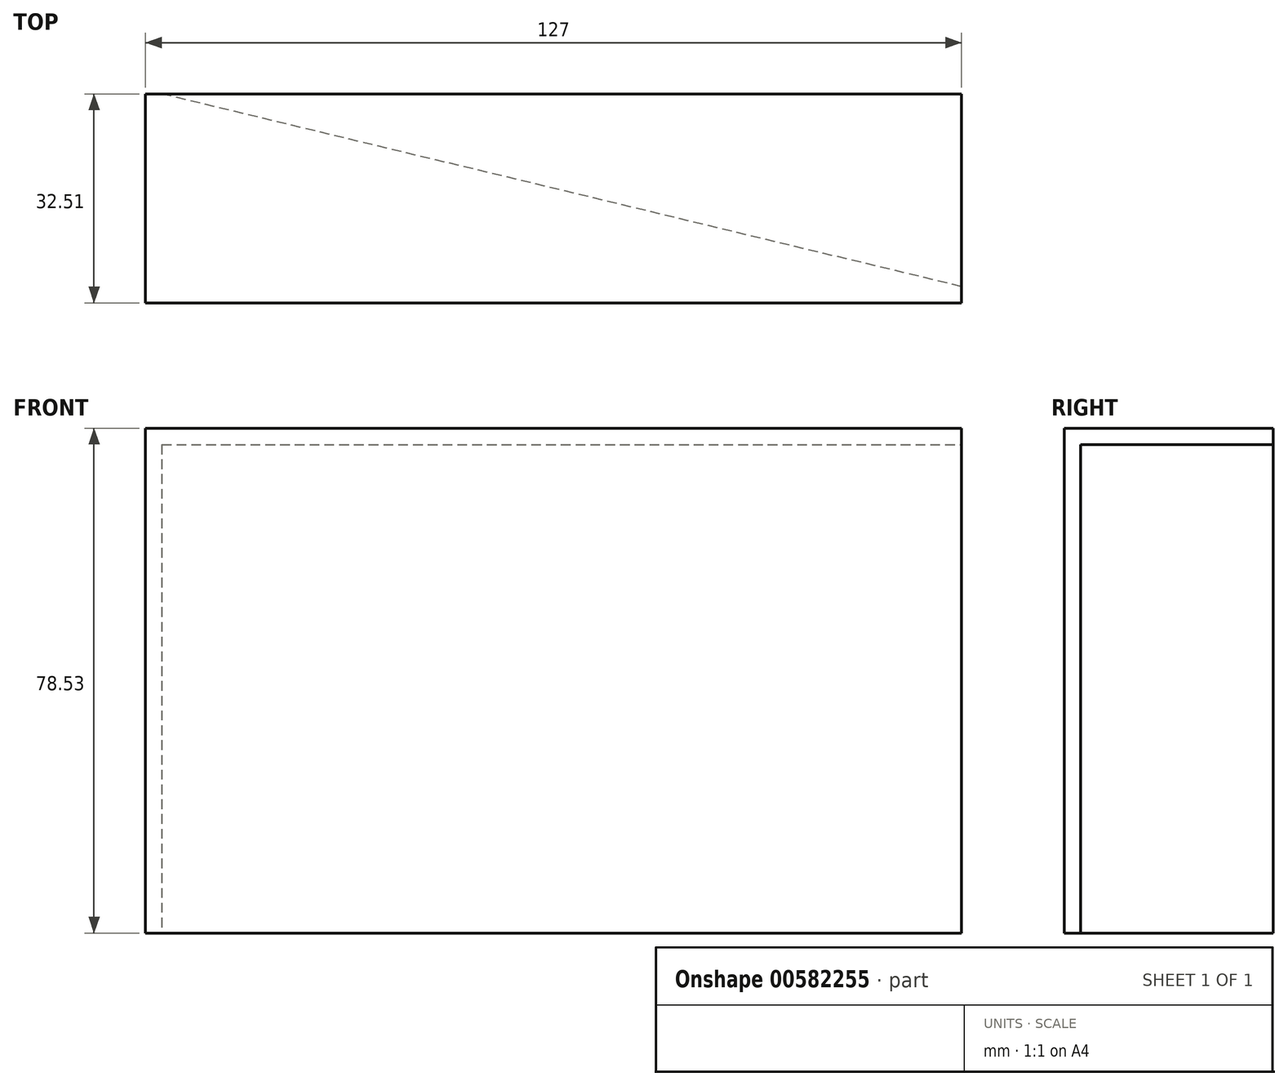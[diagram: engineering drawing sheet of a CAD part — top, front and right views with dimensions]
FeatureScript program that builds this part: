
annotation { "Feature Type Name" : "Feature", "Feature Type Description" : "" }
export const myFeature = defineFeature(function(context is Context, id is Id, definition is map)
    precondition{}
    {
        {
            var Q0;
            Q0=qCreatedBy(makeId("Front.planeOp"),FACE);
            var sketch = newSketch(context, id + "F0", { "sketchPlane" : qUnion([Q0])});
            skLineSegment(sketch, "E0.bottom", {"start": v(-105.52, 15.53) * mm, "end": v(21.48, 15.53) * mm});
            skLineSegment(sketch, "E0.top", {"start": v(-105.52, -63) * mm, "end": v(21.48, -63) * mm});
            skLineSegment(sketch, "E0.left", {"start": v(-105.52, 15.53) * mm, "end": v(-105.52, -63) * mm});
            skLineSegment(sketch, "E0.right", {"start": v(21.48, 15.53) * mm, "end": v(21.48, -63) * mm});
            skLineSegment(sketch, "E1.bottom", {"start": v(31.64, 69.27) * mm, "end": v(100.9, 69.27) * mm});
            skLineSegment(sketch, "E1.top", {"start": v(31.64, 28.83) * mm, "end": v(100.9, 28.83) * mm});
            skLineSegment(sketch, "E1.left", {"start": v(31.64, 69.27) * mm, "end": v(31.64, 28.83) * mm});
            skLineSegment(sketch, "E1.right", {"start": v(100.9, 69.27) * mm, "end": v(100.9, 28.83) * mm});
            skLineSegment(sketch, "E2", {"start": v(-105.52, 15.53) * mm, "end": v(31.64, 69.27) * mm});
            skLineSegment(sketch, "E3", {"start": v(21.48, 15.53) * mm, "end": v(31.64, 28.83) * mm});
            skSolve(sketch);
        }
        {
            var Q0;
            Q0=makeQuery(id+"F0.imprint","IMPRINT",FACE,{"disambiguationData":[TD([[makeQuery(id+"F0.imprint","IMPRINT",EDGE,{"derivedFrom":sQuery(id+"F0.wireOp",EDGE,"E0.bottom")}),-1.0]])]});
            extrude(context, id + "F1", {"entities" : qUnion([Q0]), "depth" : 32.5 * mm, "offsetDistance" : 25.4 * mm});
        }
        {
            var Q0;
            Q0=makeQuery(id+"F1.opExtrude","SWEPT_FACE",FACE,{"disambiguationData":[OSD([sQuery(id+"F0.wireOp",EDGE,"E0.right")])]});
            var Q1;
            Q1=makeQuery(id+"F1.opExtrude","SWEPT_FACE",FACE,{"disambiguationData":[OSD([sQuery(id+"F0.wireOp",EDGE,"E0.top")])]});
            var Q2;
            Q2=makeQuery(id+"F1.opExtrude","CAP_FACE",FACE,{"disambiguationData":[OSD([sQuery(id+"F0.wireOp",EDGE,"E0.bottom"),sQuery(id+"F0.wireOp",EDGE,"E0.top"),sQuery(id+"F0.wireOp",EDGE,"E0.left"),sQuery(id+"F0.wireOp",EDGE,"E0.right")])],"isStart":true});
            shell(context, id + "F2", {"entities" : qUnion([Q0, Q1, Q2]), "thickness" : 2.54 * mm});
        }
        {
            var Q1;
            Q1=makeQuery(id+"F2.opShell","OFFSET_FACE",FACE,{"disambiguationData":[OSD([sQuery(id+"F0.wireOp",EDGE,"E0.bottom"),sQuery(id+"F0.wireOp",EDGE,"E0.top"),sQuery(id+"F0.wireOp",EDGE,"E0.left"),sQuery(id+"F0.wireOp",EDGE,"E0.right")])]});
            var Q2;
            Q2=makeQuery(id+"F2.opShell","OFFSET_FACE",FACE,{"disambiguationData":[OSD([sQuery(id+"F0.wireOp",EDGE,"E0.left")])]});
            loft(context, id + "F3", {"operationType" : NewBodyOperationType.ADD, "sheetProfilesArray" : [{ "sheetProfileEntities" : qUnion([Q1]) }, { "sheetProfileEntities" : qUnion([Q2]) }]});
        }
    });
